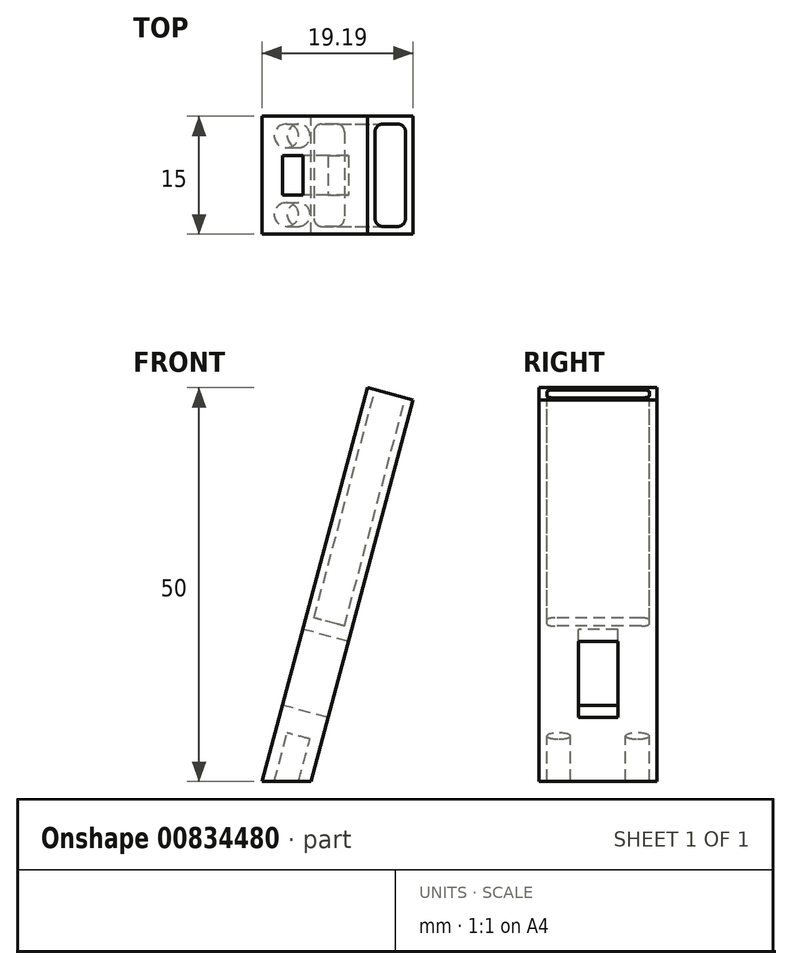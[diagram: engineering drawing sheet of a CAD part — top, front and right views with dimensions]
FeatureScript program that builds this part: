
annotation { "Feature Type Name" : "Feature", "Feature Type Description" : "" }
export const myFeature = defineFeature(function(context is Context, id is Id, definition is map)
    precondition{}
    {
        {
            var Q0;
            Q0=qCreatedBy(makeId("Front.planeOp"),FACE);
            var sketch = newSketch(context, id + "F0", { "sketchPlane" : qUnion([Q0])});
            skLineSegment(sketch, "E0", {"start": v(0, 0) * mm, "end": v(6.21, 0) * mm});
            skLineSegment(sketch, "E1", {"start": v(13.4, 50) * mm, "end": v(0, 0) * mm});
            skLineSegment(sketch, "E2", {"start": v(6.21, 0) * mm, "end": v(19.2, 48.45) * mm});
            skLineSegment(sketch, "E3", {"start": v(13.4, 50) * mm, "end": v(19.2, 48.45) * mm});
            skSolve(sketch);
        }
        {
            var Q0;
            Q0=makeQuery(id+"F0.imprint","IMPRINT",FACE,{"disambiguationData":[TD([[makeQuery(id+"F0.imprint","IMPRINT",EDGE,{"derivedFrom":sQuery(id+"F0.wireOp",EDGE,"E0")}),1.0]])]});
            extrude(context, id + "F1", {"entities" : qUnion([Q0]), "depth" : 15 * mm, "offsetDistance" : 25 * mm});
        }
        {
            var Q0;
            Q0=makeQuery(id+"F1.opExtrude","SWEPT_FACE",FACE,{"disambiguationData":[OSD([sQuery(id+"F0.wireOp",EDGE,"E3")])]});
            var sketch = newSketch(context, id + "F2", { "sketchPlane" : qUnion([Q0])});
            skLineSegment(sketch, "E4", {"start": v(3, -15) * mm, "end": v(3, 0) * mm, "construction": true});
            skCircle(sketch, "E5", {"center": v(3, -12.5) * mm, "radius": 1.5 * mm});
            skCircle(sketch, "E6", {"center": v(3, -2.5) * mm, "radius": 1.5 * mm});
            skPoint(sketch, "E7", {"position": v(3, -7.5) * mm});
            skSolve(sketch);
        }
        {
            var Q0;
            Q0=makeQuery(id+"F2.imprint","IMPRINT",FACE,{"disambiguationData":[TD([[makeQuery(id+"F2.imprint","IMPRINT",EDGE,{"derivedFrom":sQuery(id+"F2.wireOp",EDGE,"E5")}),1.0]])]});
            var Q1;
            Q1=makeQuery(id+"F2.imprint","IMPRINT",FACE,{"disambiguationData":[TD([[makeQuery(id+"F2.imprint","IMPRINT",EDGE,{"derivedFrom":sQuery(id+"F2.wireOp",EDGE,"E6")}),1.0]])]});
            extrude(context, id + "F3", {"entities" : qUnion([Q0, Q1]), "operationType" : NewBodyOperationType.REMOVE, "oppositeDirection" : true, "depth" : 55 * mm, "offsetDistance" : 25 * mm, "hasSecondDirection" : true, "secondDirectionOppositeDirection" : true, "secondDirectionDepth" : 45 * mm});
        }
        {
            var Q0;
            Q0=makeQuery(id+"F1.opExtrude","SWEPT_FACE",FACE,{"disambiguationData":[OSD([sQuery(id+"F0.wireOp",EDGE,"E3")])]});
            var sketch = newSketch(context, id + "F4", { "sketchPlane" : qUnion([Q0])});
            skLineSegment(sketch, "E8.bottom", {"start": v(5, -1) * mm, "end": v(1, -1) * mm});
            skLineSegment(sketch, "E8.top", {"start": v(5, -14) * mm, "end": v(1, -14) * mm});
            skLineSegment(sketch, "E8.left", {"start": v(5, -1) * mm, "end": v(5, -14) * mm});
            skLineSegment(sketch, "E8.right", {"start": v(1, -1) * mm, "end": v(1, -14) * mm});
            skPoint(sketch, "E8.middle", {"position": v(3, -7.5) * mm});
            skLineSegment(sketch, "E9", {"start": v(6, 0) * mm, "end": v(0, -15) * mm, "construction": true});
            skSolve(sketch);
        }
        {
            var Q0;
            Q0=makeQuery(id+"F4.imprint","IMPRINT",FACE,{"disambiguationData":[TD([[makeQuery(id+"F4.imprint","IMPRINT",EDGE,{"derivedFrom":sQuery(id+"F4.wireOp",EDGE,"E8.bottom")}),1.0]])]});
            extrude(context, id + "F5", {"entities" : qUnion([Q0]), "operationType" : NewBodyOperationType.REMOVE, "oppositeDirection" : true, "depth" : 30 * mm, "offsetDistance" : 25 * mm});
        }
        {
            var Q0;
            Q0=makeQuery(id+"F1.opExtrude","SWEPT_FACE",FACE,{"disambiguationData":[OSD([sQuery(id+"F0.wireOp",EDGE,"E1")])]});
            var sketch = newSketch(context, id + "F6", { "sketchPlane" : qUnion([Q0])});
            skLineSegment(sketch, "E10.bottom", {"start": v(5, 10) * mm, "end": v(10, 10) * mm});
            skLineSegment(sketch, "E10.top", {"start": v(5, 20) * mm, "end": v(10, 20) * mm});
            skLineSegment(sketch, "E10.left", {"start": v(5, 10) * mm, "end": v(5, 20) * mm});
            skLineSegment(sketch, "E10.right", {"start": v(10, 10) * mm, "end": v(10, 20) * mm});
            skPoint(sketch, "E10.middle", {"position": v(7.5, 15) * mm});
            skLineSegment(sketch, "E11", {"start": v(0, 15) * mm, "end": v(15, 15) * mm, "construction": true});
            skSolve(sketch);
        }
        {
            var Q0;
            Q0=makeQuery(id+"F6.imprint","IMPRINT",FACE,{"disambiguationData":[TD([[makeQuery(id+"F6.imprint","IMPRINT",EDGE,{"derivedFrom":sQuery(id+"F6.wireOp",EDGE,"E10.bottom")}),1.0]])]});
            extrude(context, id + "F7", {"entities" : qUnion([Q0]), "operationType" : NewBodyOperationType.REMOVE, "endBound" : BoundingType.THROUGH_ALL, "oppositeDirection" : true, "depth" : 25 * mm, "offsetDistance" : 25 * mm});
        }
        {
            var Q0;
            Q0=makeQuery(id+"F5.boolean.opBoolean","COPY",EDGE,{"derivedFrom":makeQuery(id+"F5.opExtrude","SWEPT_EDGE",EDGE,{"disambiguationData":[OSD([sQuery(id+"F4.wireOp",EDGE,"E8.bottom"),sQuery(id+"F4.wireOp",EDGE,"E8.right")])]})});
            var Q1;
            Q1=makeQuery(id+"F5.boolean.opBoolean","COPY",EDGE,{"derivedFrom":makeQuery(id+"F5.opExtrude","SWEPT_EDGE",EDGE,{"disambiguationData":[OSD([sQuery(id+"F4.wireOp",EDGE,"E8.top"),sQuery(id+"F4.wireOp",EDGE,"E8.left")])]})});
            var Q2;
            Q2=makeQuery(id+"F5.boolean.opBoolean","COPY",EDGE,{"derivedFrom":makeQuery(id+"F5.opExtrude","SWEPT_EDGE",EDGE,{"disambiguationData":[OSD([sQuery(id+"F4.wireOp",EDGE,"E8.top"),sQuery(id+"F4.wireOp",EDGE,"E8.right")])]})});
            var Q3;
            Q3=makeQuery(id+"F5.boolean.opBoolean","COPY",EDGE,{"derivedFrom":makeQuery(id+"F5.opExtrude","SWEPT_EDGE",EDGE,{"disambiguationData":[OSD([sQuery(id+"F4.wireOp",EDGE,"E8.bottom"),sQuery(id+"F4.wireOp",EDGE,"E8.left")])]})});
            fillet(context, id + "F8", {"entities" : qUnion([Q0, Q1, Q2, Q3]), "radius" : 1 * mm, "tangentPropagation" : true, "allowEdgeOverflow" : false});
        }
    });
